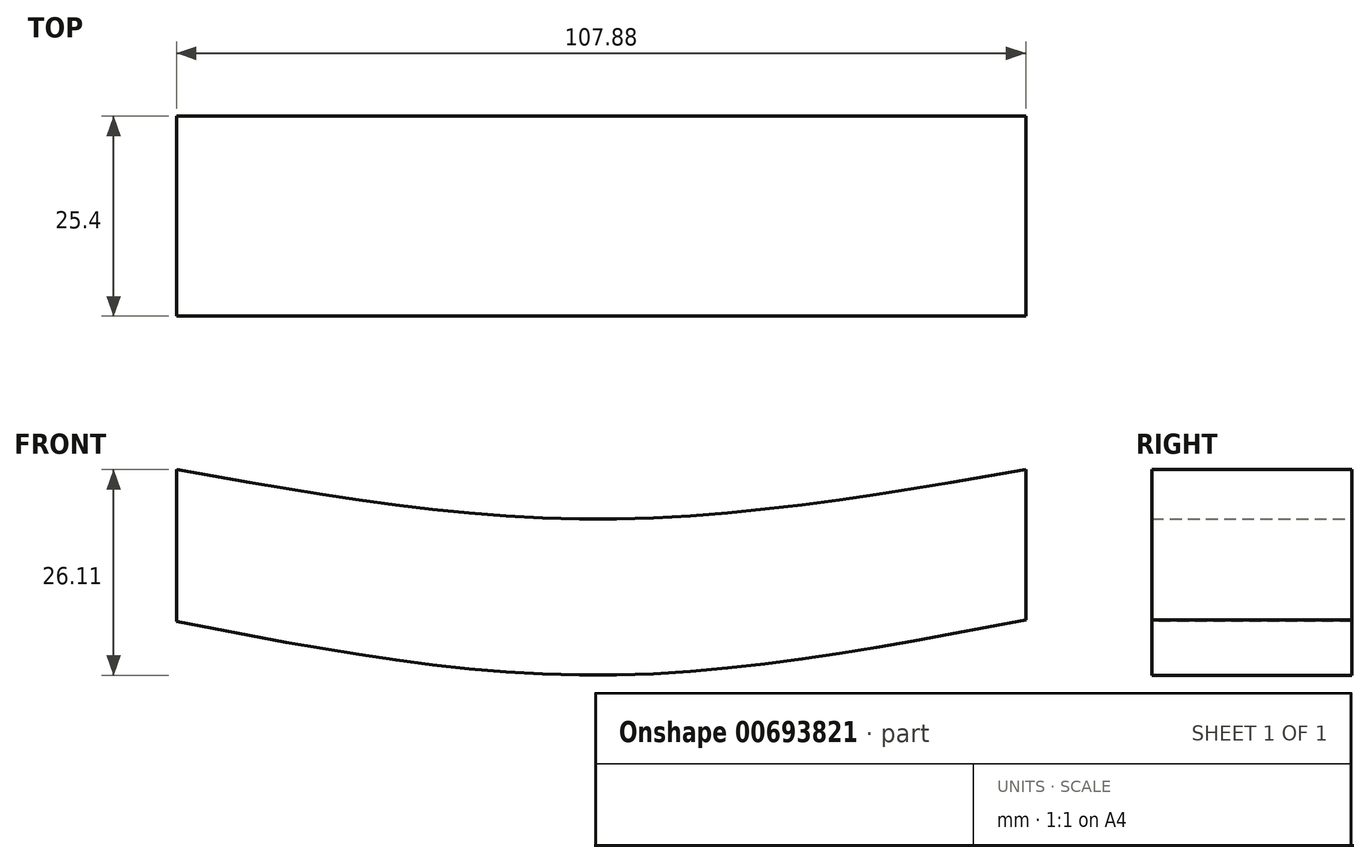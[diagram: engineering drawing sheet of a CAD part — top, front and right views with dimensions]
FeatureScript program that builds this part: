
annotation { "Feature Type Name" : "Feature", "Feature Type Description" : "" }
export const myFeature = defineFeature(function(context is Context, id is Id, definition is map)
    precondition{}
    {
        {
            var Q0;
            Q0=qCreatedBy(makeId("Front.planeOp"),FACE);
            var sketch = newSketch(context, id + "F0", { "sketchPlane" : qUnion([Q0])});
            skLineSegment(sketch, "E0.bottom", {"start": v(-53.15, 13.45) * mm, "end": v(54.73, 13.45) * mm});
            skLineSegment(sketch, "E0.top", {"start": v(-53.15, -12.66) * mm, "end": v(54.73, -12.66) * mm});
            skLineSegment(sketch, "E0.left", {"start": v(-53.15, 13.45) * mm, "end": v(-53.15, -12.66) * mm});
            skLineSegment(sketch, "E0.right", {"start": v(54.73, 13.45) * mm, "end": v(54.73, -12.66) * mm});
            skSolve(sketch);
        }
        {
            var Q0;
            Q0=makeQuery(id+"F0.imprint","IMPRINT",FACE,{"disambiguationData":[TD([[makeQuery(id+"F0.imprint","IMPRINT",EDGE,{"derivedFrom":sQuery(id+"F0.wireOp",EDGE,"E0.bottom")}),-1.0]])]});
            extrude(context, id + "F1", {"entities" : qUnion([Q0]), "depth" : 12.7 * mm, "offsetDistance" : 25.4 * mm});
        }
        {
            var Q0;
            Q0=makeQuery(id+"F1.opExtrude","CAP_FACE",FACE,{"disambiguationData":[OSD([sQuery(id+"F0.wireOp",EDGE,"E0.bottom"),sQuery(id+"F0.wireOp",EDGE,"E0.top"),sQuery(id+"F0.wireOp",EDGE,"E0.left"),sQuery(id+"F0.wireOp",EDGE,"E0.right")])],"isStart":true});
            extrude(context, id + "F2", {"entities" : qUnion([Q0]), "operationType" : NewBodyOperationType.ADD, "depth" : 12.7 * mm, "offsetDistance" : 25.4 * mm});
        }
        {
            var Q0;
            Q0=makeQuery(id+"F1.opExtrude","CAP_FACE",FACE,{"disambiguationData":[OSD([sQuery(id+"F0.wireOp",EDGE,"E0.bottom"),sQuery(id+"F0.wireOp",EDGE,"E0.top"),sQuery(id+"F0.wireOp",EDGE,"E0.left"),sQuery(id+"F0.wireOp",EDGE,"E0.right")])],"isStart":false});
            var sketch = newSketch(context, id + "F3", { "sketchPlane" : qUnion([Q0])});
            skFitSpline(sketch, "E1", {"points": [v(54.73, 13.45) * mm, v(0, 7.18) * mm, v(-53.15, 13.45) * mm], "startDerivative": vector(-109.08, -18.76) * mm, "endDerivative": vector(-106.67, 18.86) * mm});
            skPoint(sketch, "E2.1.internal.snap0", {"position": v(0.8, -12.66) * mm});
            skFitSpline(sketch, "E2", {"points": [v(-53.15, -5.83) * mm, v(0, -12.66) * mm, v(54.73, -5.63) * mm], "startDerivative": vector(106.68, -20.63) * mm, "endDerivative": vector(109.06, 20.92) * mm});
            skSolve(sketch);
        }
        {
            var Q0;
            {var subQ0=sQuery(id+"F3.wireOp",EDGE,"E2");var subQ1=makeQuery(id+"F1.opExtrude","CAP_EDGE",EDGE,{"disambiguationData":[OSD([sQuery(id+"F0.wireOp",EDGE,"E0.left")])],"isStart":false});var subQ2=makeQuery(id+"F3.imprint","INTERSECT",VERTEX,{"derivedFrom":[subQ1,subQ0]});Q0=makeQuery(id+"F3.imprint","IMPRINT",FACE,{"disambiguationData":[TD([[makeQuery(id+"F3.imprint","IMPRINT",EDGE,{"disambiguationData":[TD([[subQ2,-1.0]])],"derivedFrom":subQ0}),-1.0]])]});}
            var Q1;
            {var subQ0=sQuery(id+"F3.wireOp",EDGE,"E2");var subQ1=makeQuery(id+"F1.opExtrude","CAP_EDGE",EDGE,{"disambiguationData":[OSD([sQuery(id+"F0.wireOp",EDGE,"E0.right")])],"isStart":false});var subQ2=makeQuery(id+"F3.imprint","INTERSECT",VERTEX,{"derivedFrom":[subQ1,subQ0]});Q1=makeQuery(id+"F3.imprint","IMPRINT",FACE,{"disambiguationData":[TD([[makeQuery(id+"F3.imprint","IMPRINT",EDGE,{"disambiguationData":[TD([[subQ2,1.0]])],"derivedFrom":subQ0}),-1.0]])]});}
            var Q2;
            Q2=makeQuery(id+"F3.imprint","IMPRINT",FACE,{"disambiguationData":[TD([[makeQuery(id+"F3.imprint","IMPRINT",EDGE,{"derivedFrom":sQuery(id+"F3.wireOp",EDGE,"E1")}),-1.0]])]});
            extrude(context, id + "F4", {"entities" : qUnion([Q0, Q1, Q2]), "operationType" : NewBodyOperationType.REMOVE, "oppositeDirection" : true, "depth" : 25.4 * mm, "offsetDistance" : 25.4 * mm});
        }
    });
